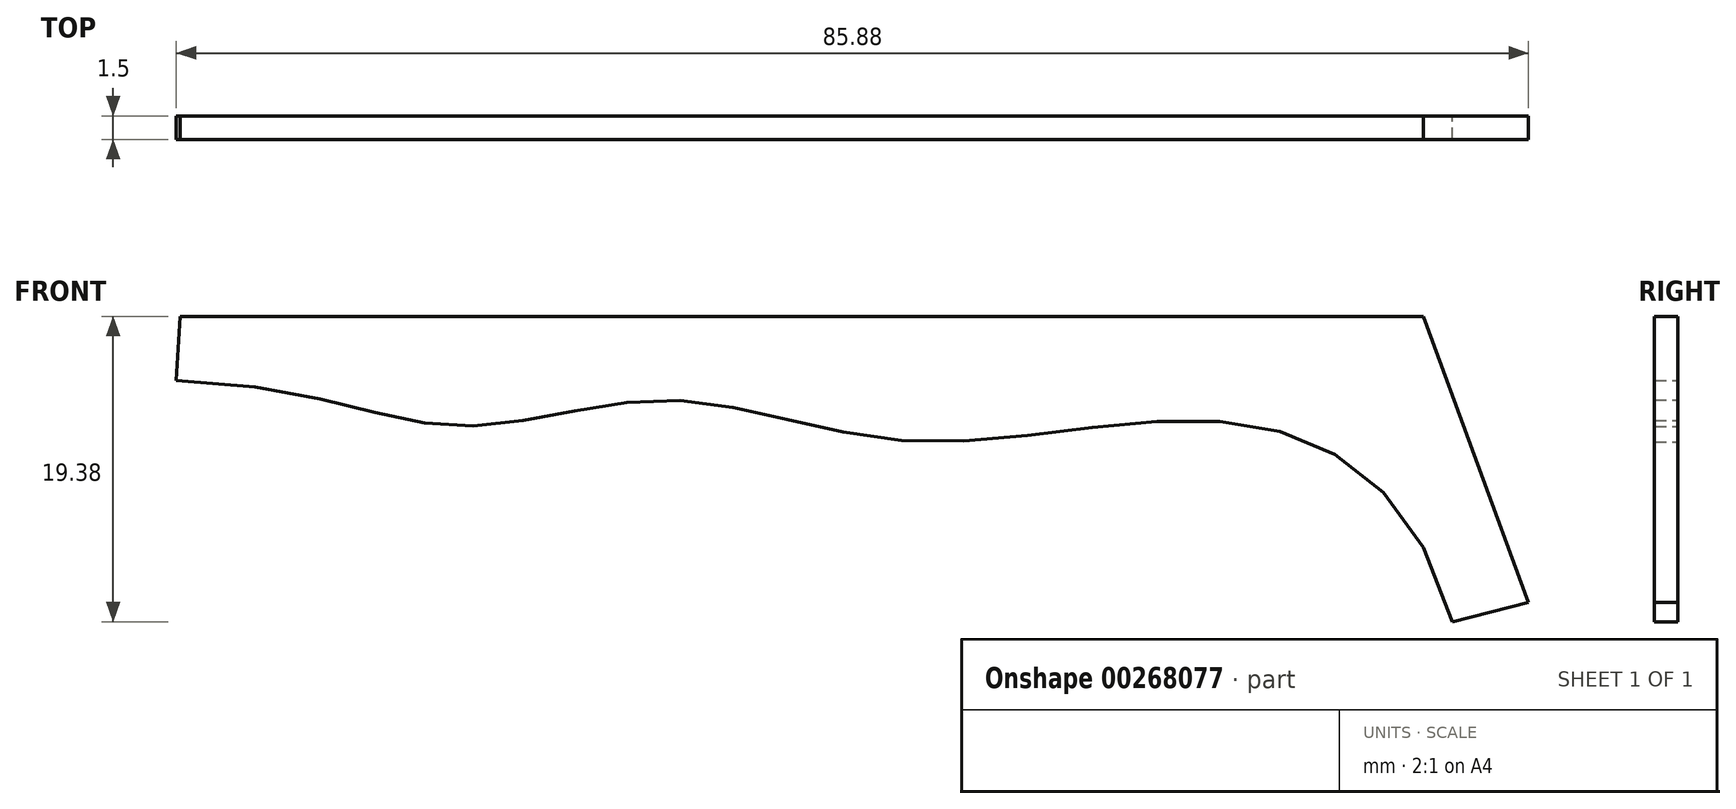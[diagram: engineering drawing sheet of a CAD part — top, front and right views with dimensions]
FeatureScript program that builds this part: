
annotation { "Feature Type Name" : "Feature", "Feature Type Description" : "" }
export const myFeature = defineFeature(function(context is Context, id is Id, definition is map)
    precondition{}
    {
        {
            var Q0;
            Q0=qCreatedBy(makeId("Front.planeOp"),FACE);
            var sketch = newSketch(context, id + "F0", { "sketchPlane" : qUnion([Q0])});
            skLineSegment(sketch, "E0", {"start": v(0, 0) * mm, "end": v(-78.96, 0) * mm});
            skLineSegment(sketch, "E1", {"start": v(-78.96, 0) * mm, "end": v(-79.22, -4.05) * mm});
            skLineSegment(sketch, "E2", {"start": v(0, 0) * mm, "end": v(6.66, -18.15) * mm});
            skLineSegment(sketch, "E3", {"start": v(6.66, -18.15) * mm, "end": v(1.84, -19.38) * mm});
            skFitSpline(sketch, "E4", {"points": [v(-79.22, -4.05) * mm, v(-61.18, -6.97) * mm, v(-47.93, -5.3) * mm, v(-32.43, -7.93) * mm, v(-12.24, -6.72) * mm, v(1.84, -19.38) * mm], "startDerivative": vector(127.47, -3.02) * mm, "endDerivative": vector(34.22, -124.07) * mm});
            skSolve(sketch);
        }
        {
            var Q0;
            Q0 = qSketchRegion(id + "F0", true);
            extrude(context, id + "F1", {"entities" : qUnion([Q0]), "depth" : 1.5 * mm});
        }
    });
